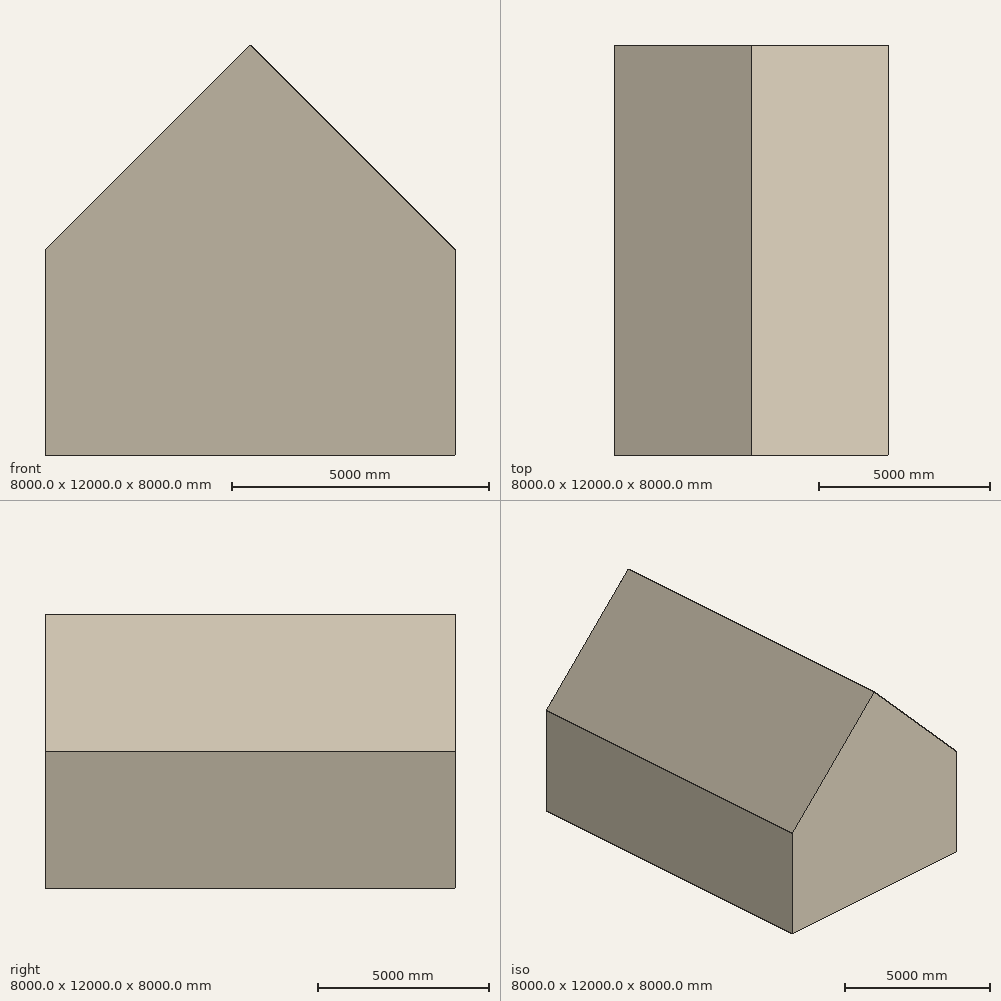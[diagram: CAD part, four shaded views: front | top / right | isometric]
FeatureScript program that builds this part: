
annotation { "Feature Type Name" : "Feature", "Feature Type Description" : "" }
export const myFeature = defineFeature(function(context is Context, id is Id, definition is map)
    precondition{}
    {
        {
            var Q0;
            Q0=qCreatedBy(makeId("Front.planeOp"),FACE);
            var sketch = newSketch(context, id + "F0", { "sketchPlane" : qUnion([Q0])});
            skLineSegment(sketch, "E0", {"start": v(0, 0) * mm, "end": v(0, -4000) * mm});
            skLineSegment(sketch, "E1", {"start": v(0, -4000) * mm, "end": v(8000, -4000) * mm});
            skLineSegment(sketch, "E2", {"start": v(8000, -4000) * mm, "end": v(8000, 0) * mm});
            skLineSegment(sketch, "E3", {"start": v(0, 0) * mm, "end": v(4000, 4000) * mm});
            skLineSegment(sketch, "E4", {"start": v(4000, 4000) * mm, "end": v(8000, 0) * mm});
            skSolve(sketch);
        }
        {
            var Q0;
            Q0 = qSketchRegion(id + "F0", true);
            extrude(context, id + "F1", {"entities" : qUnion([Q0]), "depth" : 12000 * mm});
        }
    });
